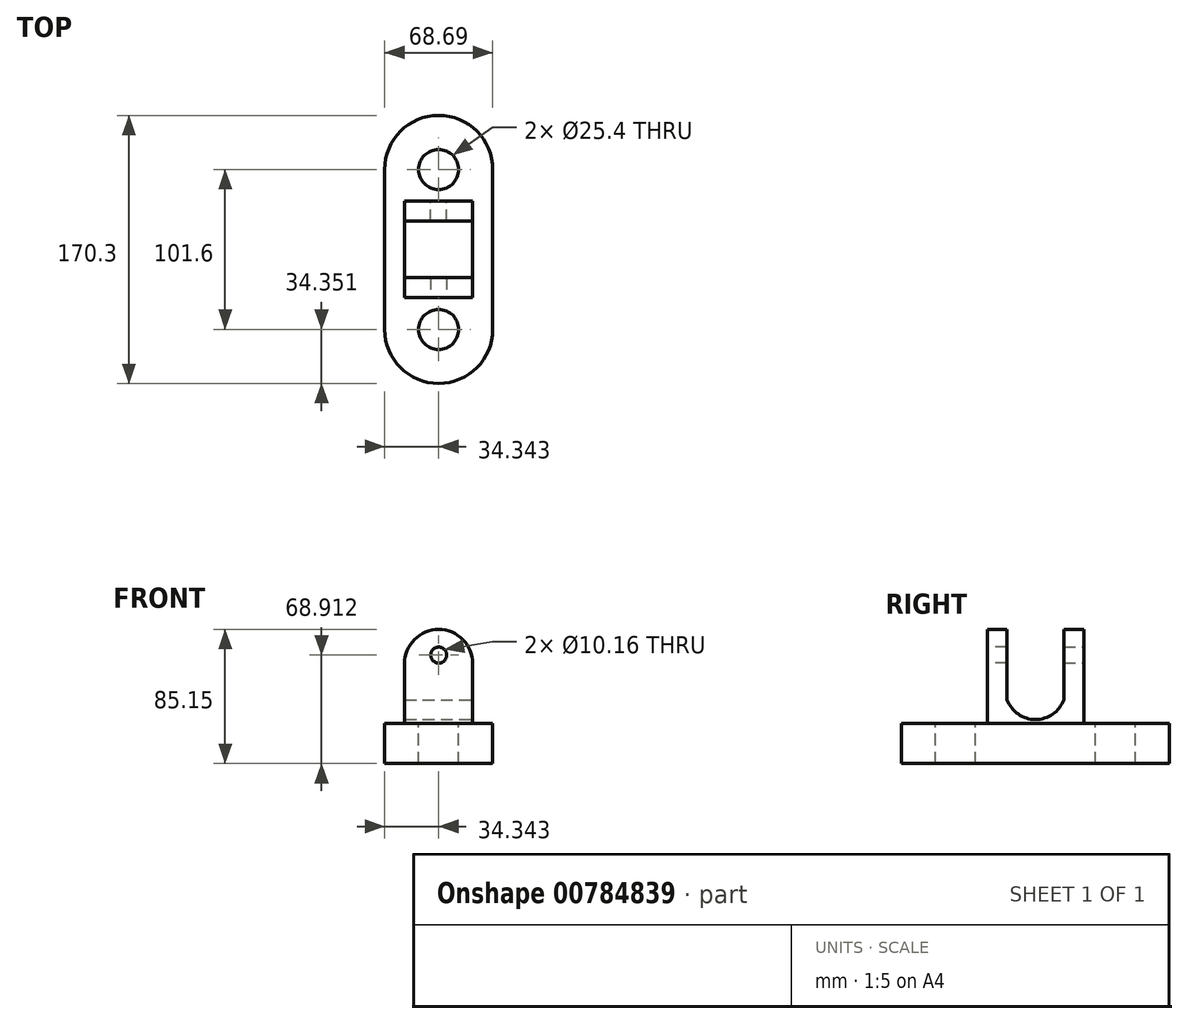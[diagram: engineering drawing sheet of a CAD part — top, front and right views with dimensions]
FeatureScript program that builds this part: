
annotation { "Feature Type Name" : "Feature", "Feature Type Description" : "" }
export const myFeature = defineFeature(function(context is Context, id is Id, definition is map)
    precondition{}
    {
        {
            var Q0;
            Q0=qCreatedBy(makeId("Top.planeOp"),FACE);
            var sketch = newSketch(context, id + "F0", { "sketchPlane" : qUnion([Q0])});
            skLineSegment(sketch, "E0", {"start": v(0, 0) * mm, "end": v(0, 46.25) * mm});
            skLineSegment(sketch, "E1", {"start": v(0, 0) * mm, "end": v(0, -55.35) * mm});
            skLineSegment(sketch, "E2", {"start": v(-68.7, 46.25) * mm, "end": v(-68.7, -55.35) * mm});
            skArc(sketch, "E3", {"start": v(0, 46.25) * mm, "mid": v(-34.35, 80.6) * mm, "end": v(-68.7, 46.25) * mm});
            skArc(sketch, "E4", {"start": v(-68.7, -55.35) * mm, "mid": v(-34.35, -89.7) * mm, "end": v(0, -55.35) * mm});
            skCircle(sketch, "E5", {"center": v(-34.35, 46.25) * mm, "radius": 12.7 * mm});
            skCircle(sketch, "E6", {"center": v(-34.35, -55.35) * mm, "radius": 12.7 * mm});
            skSolve(sketch);
        }
        {
            var Q0;
            Q0=makeQuery(id+"F0.imprint","IMPRINT",FACE,{"disambiguationData":[TD([[makeQuery(id+"F0.imprint","IMPRINT",EDGE,{"derivedFrom":sQuery(id+"F0.wireOp",EDGE,"c1GTwHII-aoyZ-vGL7-lIDA-Nu8VCe8G4Fbm")}),1.0]])]});
            var Q1;
            Q1=makeQuery(id+"F0.imprint","IMPRINT",FACE,{"disambiguationData":[TD([[makeQuery(id+"F0.imprint","IMPRINT",EDGE,{"derivedFrom":sQuery(id+"F0.wireOp",EDGE,"E0")}),1.0]])]});
            extrude(context, id + "F1", {"entities" : qUnion([Q0, Q1]), "oppositeDirection" : true, "depth" : 25.4 * mm, "offsetDistance" : 25.4 * mm});
        }
        {
            var Q0;
            Q0=makeQuery(id+"F1.opExtrude","CAP_FACE",FACE,{"disambiguationData":[OSD([sQuery(id+"F0.wireOp",EDGE,"E0"),sQuery(id+"F0.wireOp",EDGE,"E1"),sQuery(id+"F0.wireOp",EDGE,"E2"),sQuery(id+"F0.wireOp",EDGE,"E3"),sQuery(id+"F0.wireOp",EDGE,"E4"),sQuery(id+"F0.wireOp",EDGE,"E5"),sQuery(id+"F0.wireOp",EDGE,"E6")])],"isStart":true});
            var sketch = newSketch(context, id + "F2", { "sketchPlane" : qUnion([Q0])});
            skLineSegment(sketch, "E7", {"start": v(-56, -4.55) * mm, "end": v(-56, -35.23) * mm});
            skLineSegment(sketch, "E8", {"start": v(-56, -35.23) * mm, "end": v(-12.7, -35.23) * mm});
            skLineSegment(sketch, "E9", {"start": v(-12.7, -35.23) * mm, "end": v(-12.7, -4.55) * mm});
            skLineSegment(sketch, "E10.MirrorCS", {"start": v(-12.7, 26.13) * mm, "end": v(-12.7, -4.55) * mm});
            skLineSegment(sketch, "E11.MirrorCS", {"start": v(-56, -4.55) * mm, "end": v(-56, 26.13) * mm});
            skLineSegment(sketch, "E12.MirrorCS", {"start": v(-56, 26.13) * mm, "end": v(-12.7, 26.13) * mm});
            skSolve(sketch);
        }
        {
            var Q0;
            Q0=makeQuery(id+"F2.imprint","IMPRINT",FACE,{"disambiguationData":[TD([[makeQuery(id+"F2.imprint","IMPRINT",EDGE,{"derivedFrom":sQuery(id+"F2.wireOp",EDGE,"E7")}),1.0]])]});
            extrude(context, id + "F3", {"entities" : qUnion([Q0]), "operationType" : NewBodyOperationType.ADD, "depth" : 38.1 * mm, "offsetDistance" : 25.4 * mm});
        }
        {
            var Q0;
            Q0=makeQuery(id+"F3.opExtrude","SWEPT_FACE",FACE,{"disambiguationData":[OSD([sQuery(id+"F2.wireOp",EDGE,"E9"),sQuery(id+"F2.wireOp",EDGE,"E10.MirrorCS")])]});
            var sketch = newSketch(context, id + "F4", { "sketchPlane" : qUnion([Q0])});
            skLineSegment(sketch, "E13", {"start": v(-35.23, 38.1) * mm, "end": v(-22.53, 38.1) * mm});
            skLineSegment(sketch, "E14", {"start": v(26.13, 38.1) * mm, "end": v(13.43, 38.1) * mm});
            skLineSegment(sketch, "E15", {"start": v(-22.53, 38.1) * mm, "end": v(-22.53, 15.04) * mm});
            skLineSegment(sketch, "E16", {"start": v(13.43, 38.1) * mm, "end": v(13.43, 15.04) * mm});
            skArc(sketch, "E17", {"start": v(-22.53, 15.04) * mm, "mid": v(-4.55, 2.55) * mm, "end": v(13.43, 15.04) * mm});
            skSolve(sketch);
        }
        {
            var Q0;
            {var subQ0=sQuery(id+"F4.wireOp",EDGE,"E15");Q0=makeQuery(id+"F4.imprint","IMPRINT",FACE,{"disambiguationData":[TD([[makeQuery(id+"F4.imprint","IMPRINT",EDGE,{"derivedFrom":subQ0}),1.0]])]});}
            extrude(context, id + "F5", {"entities" : qUnion([Q0]), "operationType" : NewBodyOperationType.REMOVE, "oppositeDirection" : true, "depth" : 69.1 * mm, "offsetDistance" : 25.4 * mm});
        }
        {
            var Q0;
            Q0=makeQuery(id+"F3.opExtrude","SWEPT_FACE",FACE,{"disambiguationData":[OSD([sQuery(id+"F2.wireOp",EDGE,"E8")])]});
            var sketch = newSketch(context, id + "F6", { "sketchPlane" : qUnion([Q0])});
            skArc(sketch, "E18", {"start": v(-12.7, 38.1) * mm, "mid": v(-34.35, 59.75) * mm, "end": v(-56, 38.1) * mm});
            skCircle(sketch, "E19", {"center": v(-34.35, 43.51) * mm, "radius": 5.08 * mm});
            skSolve(sketch);
        }
        {
            var Q0;
            Q0=makeQuery(id+"F3.opExtrude","SWEPT_FACE",FACE,{"disambiguationData":[OSD([sQuery(id+"F2.wireOp",EDGE,"E12.MirrorCS")])]});
            var sketch = newSketch(context, id + "F7", { "sketchPlane" : qUnion([Q0])});
            skArc(sketch, "E20", {"start": v(56, 38.1) * mm, "mid": v(34.35, 59.75) * mm, "end": v(12.7, 38.1) * mm});
            skCircle(sketch, "E21", {"center": v(34.35, 43.51) * mm, "radius": 5.08 * mm});
            skSolve(sketch);
        }
        {
            var Q0;
            Q0=makeQuery(id+"F7.imprint","IMPRINT",FACE,{"disambiguationData":[TD([[makeQuery(id+"F7.imprint","IMPRINT",EDGE,{"derivedFrom":sQuery(id+"F7.wireOp",EDGE,"E20")}),1.0]])]});
            extrude(context, id + "F8", {"entities" : qUnion([Q0]), "operationType" : NewBodyOperationType.ADD, "oppositeDirection" : true, "depth" : 12.7 * mm, "offsetDistance" : 25.4 * mm});
        }
        {
            var Q0;
            Q0=makeQuery(id+"F6.imprint","IMPRINT",FACE,{"disambiguationData":[TD([[makeQuery(id+"F6.imprint","IMPRINT",EDGE,{"derivedFrom":sQuery(id+"F6.wireOp",EDGE,"E18")}),1.0]])]});
            extrude(context, id + "F9", {"entities" : qUnion([Q0]), "operationType" : NewBodyOperationType.ADD, "oppositeDirection" : true, "depth" : 12.7 * mm, "offsetDistance" : 25.4 * mm});
        }
    });
